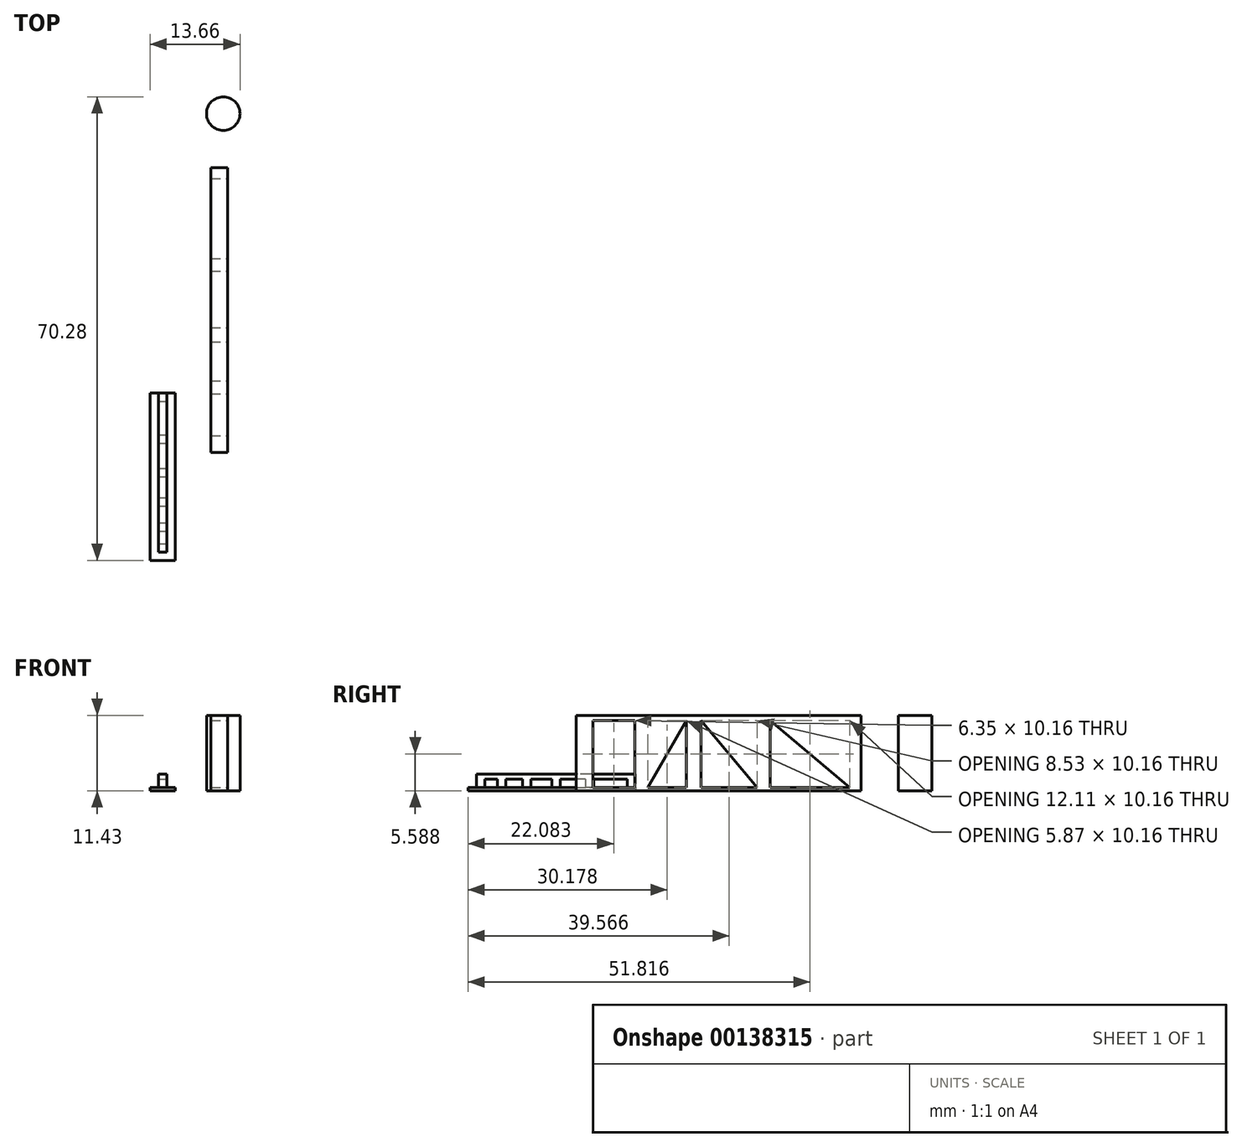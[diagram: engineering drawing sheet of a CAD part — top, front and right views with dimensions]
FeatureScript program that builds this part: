
annotation { "Feature Type Name" : "Feature", "Feature Type Description" : "" }
export const myFeature = defineFeature(function(context is Context, id is Id, definition is map)
    precondition{}
    {
        {
            var Q0;
            Q0=qCreatedBy(makeId("Top.planeOp"),FACE);
            var sketch = newSketch(context, id + "F0", { "sketchPlane" : qUnion([Q0])});
            skLineSegment(sketch, "E0.bottom", {"start": v(1.9, -12.7) * mm, "end": v(-1.9, -12.7) * mm});
            skLineSegment(sketch, "E0.top", {"start": v(1.9, 12.7) * mm, "end": v(-1.9, 12.7) * mm});
            skLineSegment(sketch, "E0.left", {"start": v(1.9, -12.7) * mm, "end": v(1.9, 12.7) * mm});
            skLineSegment(sketch, "E0.right", {"start": v(-1.9, -12.7) * mm, "end": v(-1.9, 12.7) * mm});
            skPoint(sketch, "E0.middle", {"position": v(0, 0) * mm});
            skSolve(sketch);
        }
        {
            var Q0;
            Q0 = qSketchRegion(id + "F0", true);
            extrude(context, id + "F1", {"entities" : qUnion([Q0]), "depth" : 0.5 * mm});
        }
        {
            var Q0;
            Q0=makeQuery(id+"F1.opExtrude","CAP_FACE",FACE,{"disambiguationData":[OSD([sQuery(id+"F0.wireOp",EDGE,"E0.bottom"),sQuery(id+"F0.wireOp",EDGE,"E0.top"),sQuery(id+"F0.wireOp",EDGE,"E0.left"),sQuery(id+"F0.wireOp",EDGE,"E0.right")])],"isStart":false});
            var sketch = newSketch(context, id + "F2", { "sketchPlane" : qUnion([Q0])});
            skLineSegment(sketch, "E1.bottom", {"start": v(-0.63, 12.7) * mm, "end": v(0.64, 12.7) * mm});
            skLineSegment(sketch, "E1.top", {"start": v(-0.63, 11.43) * mm, "end": v(0.64, 11.43) * mm});
            skLineSegment(sketch, "E1.left", {"start": v(-0.63, 12.7) * mm, "end": v(-0.63, 11.43) * mm});
            skLineSegment(sketch, "E1.right", {"start": v(0.64, 12.7) * mm, "end": v(0.64, 11.43) * mm});
            skPoint(sketch, "E2.firstSnap0", {"position": v(-0.63, 12.07) * mm});
            skLineSegment(sketch, "E2.bottom", {"start": v(-0.63, 6.35) * mm, "end": v(0.64, 6.35) * mm});
            skLineSegment(sketch, "E2.top", {"start": v(-0.63, 5.08) * mm, "end": v(0.64, 5.08) * mm});
            skLineSegment(sketch, "E2.left", {"start": v(-0.63, 6.35) * mm, "end": v(-0.63, 5.08) * mm});
            skLineSegment(sketch, "E2.right", {"start": v(0.64, 6.35) * mm, "end": v(0.64, 5.08) * mm});
            skLineSegment(sketch, "E3.bottom", {"start": v(-0.63, 1.27) * mm, "end": v(0.64, 1.27) * mm});
            skLineSegment(sketch, "E3.top", {"start": v(-0.63, 0) * mm, "end": v(0.64, 0) * mm});
            skLineSegment(sketch, "E3.left", {"start": v(-0.63, 1.27) * mm, "end": v(-0.63, 0) * mm});
            skLineSegment(sketch, "E3.right", {"start": v(0.64, 1.27) * mm, "end": v(0.64, 0) * mm});
            skLineSegment(sketch, "E4.bottom", {"start": v(-0.63, -3.18) * mm, "end": v(0.64, -3.18) * mm});
            skLineSegment(sketch, "E4.top", {"start": v(-0.63, -4.45) * mm, "end": v(0.64, -4.45) * mm});
            skLineSegment(sketch, "E4.left", {"start": v(-0.63, -3.18) * mm, "end": v(-0.63, -4.45) * mm});
            skLineSegment(sketch, "E4.right", {"start": v(0.64, -3.18) * mm, "end": v(0.64, -4.45) * mm});
            skLineSegment(sketch, "E5.bottom", {"start": v(-0.63, -6.99) * mm, "end": v(0.64, -6.99) * mm});
            skLineSegment(sketch, "E5.top", {"start": v(-0.63, -8.26) * mm, "end": v(0.64, -8.26) * mm});
            skLineSegment(sketch, "E5.left", {"start": v(-0.63, -6.99) * mm, "end": v(-0.63, -8.26) * mm});
            skLineSegment(sketch, "E5.right", {"start": v(0.64, -6.99) * mm, "end": v(0.64, -8.26) * mm});
            skLineSegment(sketch, "E6.bottom", {"start": v(-0.63, -10.16) * mm, "end": v(0.64, -10.16) * mm});
            skLineSegment(sketch, "E6.top", {"start": v(-0.63, -11.43) * mm, "end": v(0.64, -11.43) * mm});
            skLineSegment(sketch, "E6.left", {"start": v(-0.63, -10.16) * mm, "end": v(-0.63, -11.43) * mm});
            skLineSegment(sketch, "E6.right", {"start": v(0.64, -10.16) * mm, "end": v(0.64, -11.43) * mm});
            skSolve(sketch);
        }
        {
            var Q0;
            Q0 = qSketchRegion(id + "F2", true);
            extrude(context, id + "F3", {"entities" : qUnion([Q0]), "operationType" : NewBodyOperationType.ADD, "depth" : 1.27 * mm});
        }
        {
            var Q0;
            Q0=makeQuery(id+"F3.opExtrude","CAP_FACE",FACE,{"disambiguationData":[OSD([sQuery(id+"F2.wireOp",EDGE,"E6.bottom"),sQuery(id+"F2.wireOp",EDGE,"E6.top"),sQuery(id+"F2.wireOp",EDGE,"E6.left"),sQuery(id+"F2.wireOp",EDGE,"E6.right")])],"isStart":false});
            var sketch = newSketch(context, id + "F4", { "sketchPlane" : qUnion([Q0])});
            skLineSegment(sketch, "E7.bottom", {"start": v(0.64, -11.43) * mm, "end": v(-0.63, -11.43) * mm});
            skLineSegment(sketch, "E7.top", {"start": v(0.63, 12.7) * mm, "end": v(-0.64, 12.7) * mm});
            skLineSegment(sketch, "E7.left", {"start": v(0.64, -11.43) * mm, "end": v(0.63, 12.7) * mm});
            skLineSegment(sketch, "E7.right", {"start": v(-0.63, -11.43) * mm, "end": v(-0.64, 12.7) * mm});
            skSolve(sketch);
        }
        {
            var Q0;
            Q0 = qSketchRegion(id + "F4", true);
            extrude(context, id + "F5", {"entities" : qUnion([Q0]), "operationType" : NewBodyOperationType.ADD, "depth" : 0.76 * mm});
        }
        {
            var Q0;
            Q0=qCreatedBy(makeId("Top.planeOp"),FACE);
            var sketch = newSketch(context, id + "F6", { "sketchPlane" : qUnion([Q0])});
            skLineSegment(sketch, "E8.bottom", {"start": v(7.3, 46.85) * mm, "end": v(9.84, 46.85) * mm});
            skLineSegment(sketch, "E8.top", {"start": v(7.3, 3.67) * mm, "end": v(9.84, 3.67) * mm});
            skLineSegment(sketch, "E8.left", {"start": v(7.3, 46.85) * mm, "end": v(7.3, 3.67) * mm});
            skLineSegment(sketch, "E8.right", {"start": v(9.84, 46.85) * mm, "end": v(9.84, 3.67) * mm});
            skCircle(sketch, "E9", {"center": v(9.2, 55.04) * mm, "radius": 2.54 * mm});
            skSolve(sketch);
        }
        {
            var Q0;
            Q0 = qSketchRegion(id + "F6", true);
            extrude(context, id + "F7", {"entities" : qUnion([Q0]), "depth" : 11.43 * mm, "offsetDistance" : 25.4 * mm});
        }
        {
            var Q0;
            Q0=makeQuery(id+"F7.opExtrude","SWEPT_FACE",FACE,{"disambiguationData":[OSD([sQuery(id+"F6.wireOp",EDGE,"E8.right")])]});
            var sketch = newSketch(context, id + "F8", { "sketchPlane" : qUnion([Q0])});
            skLineSegment(sketch, "E10.bottom", {"start": v(6.2, 10.67) * mm, "end": v(12.56, 10.67) * mm});
            skLineSegment(sketch, "E10.top", {"start": v(6.2, 0.5) * mm, "end": v(12.56, 0.5) * mm});
            skLineSegment(sketch, "E10.left", {"start": v(6.2, 10.67) * mm, "end": v(6.2, 0.5) * mm});
            skLineSegment(sketch, "E10.right", {"start": v(12.56, 10.67) * mm, "end": v(12.56, 0.5) * mm});
            skLineSegment(sketch, "E11", {"start": v(14.55, 0.5) * mm, "end": v(20.41, 10.67) * mm});
            skLineSegment(sketch, "E12", {"start": v(20.41, 10.67) * mm, "end": v(20.41, 0.5) * mm});
            skLineSegment(sketch, "E13", {"start": v(20.41, 0.5) * mm, "end": v(14.55, 0.5) * mm});
            skLineSegment(sketch, "E14", {"start": v(22.6, 0.5) * mm, "end": v(22.6, 10.67) * mm});
            skLineSegment(sketch, "E15", {"start": v(22.6, 10.67) * mm, "end": v(31.13, 0.5) * mm});
            skLineSegment(sketch, "E16", {"start": v(31.13, 0.5) * mm, "end": v(22.6, 0.5) * mm});
            skLineSegment(sketch, "E17", {"start": v(33.06, 0.5) * mm, "end": v(33.06, 10.67) * mm});
            skLineSegment(sketch, "E18", {"start": v(33.06, 10.67) * mm, "end": v(45.17, 0.5) * mm});
            skLineSegment(sketch, "E19", {"start": v(45.17, 0.5) * mm, "end": v(33.06, 0.5) * mm});
            skSolve(sketch);
        }
        {
            var Q0;
            Q0 = qSketchRegion(id + "F8", true);
            extrude(context, id + "F9", {"entities" : qUnion([Q0]), "operationType" : NewBodyOperationType.REMOVE, "endBound" : BoundingType.UP_TO_NEXT, "oppositeDirection" : true, "depth" : 25.4 * mm, "offsetDistance" : 25.4 * mm});
        }
    });
